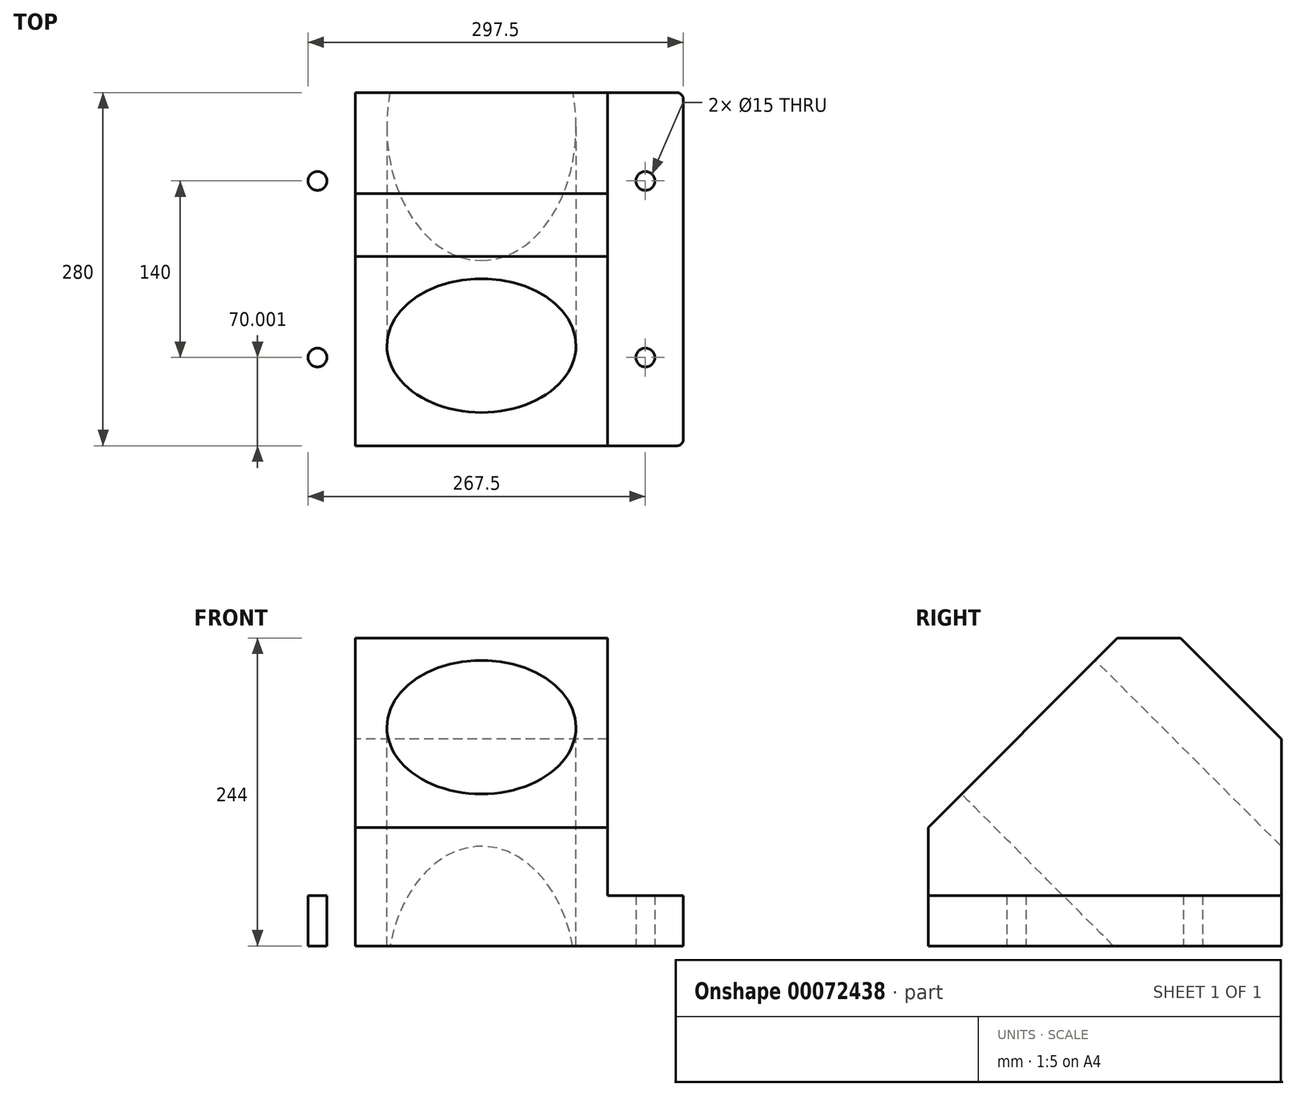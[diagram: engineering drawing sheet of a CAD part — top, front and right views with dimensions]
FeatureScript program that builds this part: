
annotation { "Feature Type Name" : "Feature", "Feature Type Description" : "" }
export const myFeature = defineFeature(function(context is Context, id is Id, definition is map)
    precondition{}
    {
        {
            var Q0;
            Q0=qCreatedBy(makeId("Right.planeOp"),FACE);
            var sketch = newSketch(context, id + "F0", { "sketchPlane" : qUnion([Q0])});
            skLineSegment(sketch, "E0", {"start": v(-129.02, 7.7) * mm, "end": v(-129.02, -86.3) * mm});
            skLineSegment(sketch, "E1", {"start": v(-129.02, -86.3) * mm, "end": v(150.98, -86.3) * mm});
            skLineSegment(sketch, "E2", {"start": v(150.98, -86.3) * mm, "end": v(150.98, 77.7) * mm});
            skLineSegment(sketch, "E3", {"start": v(150.98, 77.7) * mm, "end": v(70.98, 157.7) * mm});
            skLineSegment(sketch, "E4", {"start": v(70.98, 157.7) * mm, "end": v(20.98, 157.7) * mm});
            skLineSegment(sketch, "E5", {"start": v(20.98, 157.7) * mm, "end": v(-129.02, 7.7) * mm});
            skLineSegment(sketch, "E6", {"start": v(-129.02, -46.3) * mm, "end": v(150.98, -46.3) * mm});
            skSolve(sketch);
        }
        {
            var Q0;
            {var subQ0=sQuery(id+"F0.wireOp",EDGE,"E1");Q0=makeQuery(id+"F0.imprint","IMPRINT",FACE,{"disambiguationData":[TD([[makeQuery(id+"F0.imprint","IMPRINT",EDGE,{"derivedFrom":subQ0}),1.0]])]});}
            extrude(context, id + "F1", {"entities" : qUnion([Q0]), "depth" : 320 * mm, "symmetric" : true});
        }
        {
            var Q0;
            Q0=makeQuery(id+"F1.opExtrude","CAP_EDGE",EDGE,{"disambiguationData":[OSD([sQuery(id+"F0.wireOp",EDGE,"E0")])],"isStart":false});
            var Q1;
            Q1=makeQuery(id+"F1.opExtrude","CAP_EDGE",EDGE,{"disambiguationData":[OSD([sQuery(id+"F0.wireOp",EDGE,"E0")])],"isStart":true});
            var Q2;
            Q2=makeQuery(id+"F1.opExtrude","CAP_EDGE",EDGE,{"disambiguationData":[OSD([sQuery(id+"F0.wireOp",EDGE,"E2")])],"isStart":false});
            var Q3;
            Q3=makeQuery(id+"F1.opExtrude","CAP_EDGE",EDGE,{"disambiguationData":[OSD([sQuery(id+"F0.wireOp",EDGE,"E2")])],"isStart":true});
            fillet(context, id + "F2", {"entities" : qUnion([Q0, Q1, Q2, Q3]), "radius" : 5 * mm, "tangentPropagation" : true, "allowEdgeOverflow" : false});
        }
        {
            var Q0;
            Q0=makeQuery(id+"F1.opExtrude","SWEPT_FACE",FACE,{"disambiguationData":[OSD([sQuery(id+"F0.wireOp",EDGE,"E1")])]});
            var sketch = newSketch(context, id + "F3", { "sketchPlane" : qUnion([Q0])});
            skCircle(sketch, "E7", {"center": v(130, -80.98) * mm, "radius": 7.5 * mm});
            skCircle(sketch, "E8", {"center": v(130, 59.02) * mm, "radius": 7.5 * mm});
            skLineSegment(sketch, "E9", {"start": v(100, -150.98) * mm, "end": v(100, 129.02) * mm});
            skLineSegment(sketch, "E10.MirrorCS", {"start": v(-100, -150.98) * mm, "end": v(-100, 129.02) * mm});
            skCircle(sketch, "E11.MirrorC", {"center": v(-130, -80.98) * mm, "radius": 7.5 * mm});
            skCircle(sketch, "E12.MirrorC", {"center": v(-130, 59.02) * mm, "radius": 7.5 * mm});
            skSolve(sketch);
        }
        {
            var Q0;
            Q0=makeQuery(id+"F3.imprint","IMPRINT",FACE,{"disambiguationData":[TD([[makeQuery(id+"F3.imprint","IMPRINT",EDGE,{"derivedFrom":sQuery(id+"F3.wireOp",EDGE,"E7")}),1.0]])]});
            var Q1;
            Q1=makeQuery(id+"F3.imprint","IMPRINT",FACE,{"disambiguationData":[TD([[makeQuery(id+"F3.imprint","IMPRINT",EDGE,{"derivedFrom":sQuery(id+"F3.wireOp",EDGE,"E8")}),1.0]])]});
            var Q2;
            Q2=makeQuery(id+"F3.imprint","IMPRINT",FACE,{"disambiguationData":[TD([[makeQuery(id+"F3.imprint","IMPRINT",EDGE,{"derivedFrom":sQuery(id+"F3.wireOp",EDGE,"E11.MirrorC")}),-1.0]])]});
            var Q3;
            Q3=makeQuery(id+"F3.imprint","IMPRINT",FACE,{"disambiguationData":[TD([[makeQuery(id+"F3.imprint","IMPRINT",EDGE,{"derivedFrom":sQuery(id+"F3.wireOp",EDGE,"E12.MirrorC")}),-1.0]])]});
            extrude(context, id + "F4", {"entities" : qUnion([Q0, Q1, Q2, Q3]), "operationType" : NewBodyOperationType.REMOVE, "oppositeDirection" : true, "depth" : 50 * mm});
        }
        {
            var Q0;
            {var subQ0=sQuery(id+"F0.wireOp",EDGE,"E3");Q0=makeQuery(id+"F0.imprint","IMPRINT",FACE,{"disambiguationData":[TD([[makeQuery(id+"F0.imprint","IMPRINT",EDGE,{"derivedFrom":subQ0}),1.0]])]});}
            extrude(context, id + "F5", {"entities" : qUnion([Q0]), "operationType" : NewBodyOperationType.ADD, "depth" : 200 * mm, "symmetric" : true});
        }
        {
            var Q0;
            Q0=makeQuery(id+"F5.opExtrude","SWEPT_FACE",FACE,{"disambiguationData":[OSD([sQuery(id+"F0.wireOp",EDGE,"E5")])]});
            var sketch = newSketch(context, id + "F6", { "sketchPlane" : qUnion([Q0])});
            skLineSegment(sketch, "E13", {"start": v(0, 101.59) * mm, "end": v(0, -48.41) * mm});
            skCircle(sketch, "E14", {"center": v(0, 26.59) * mm, "radius": 75 * mm});
            skSolve(sketch);
        }
        {
            var Q0;
            {var subQ0=sQuery(id+"F6.wireOp",EDGE,"E13");Q0=makeQuery(id+"F6.imprint","IMPRINT",FACE,{"disambiguationData":[TD([[makeQuery(id+"F6.imprint","IMPRINT",EDGE,{"derivedFrom":subQ0}),-1.0]])]});}
            var Q1;
            {var subQ0=sQuery(id+"F6.wireOp",EDGE,"E13");Q1=makeQuery(id+"F6.imprint","IMPRINT",FACE,{"disambiguationData":[TD([[makeQuery(id+"F6.imprint","IMPRINT",EDGE,{"derivedFrom":subQ0}),1.0]])]});}
            extrude(context, id + "F7", {"entities" : qUnion([Q0, Q1]), "operationType" : NewBodyOperationType.REMOVE, "oppositeDirection" : true, "depth" : 81751 * mm});
        }
    });
